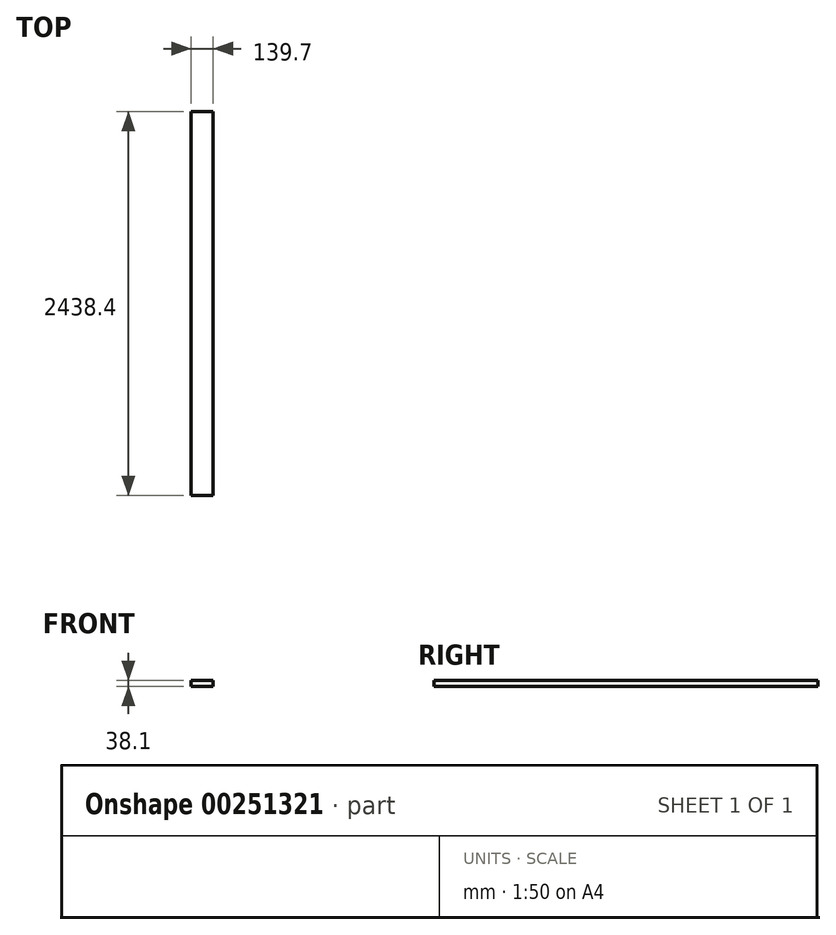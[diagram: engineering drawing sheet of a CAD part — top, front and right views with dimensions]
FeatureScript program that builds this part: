
annotation { "Feature Type Name" : "Feature", "Feature Type Description" : "" }
export const myFeature = defineFeature(function(context is Context, id is Id, definition is map)
    precondition{}
    {
        {
            var Q0;
            Q0=qCreatedBy(makeId("Top.planeOp"),FACE);
            var sketch = newSketch(context, id + "F0", { "sketchPlane" : qUnion([Q0])});
            skLineSegment(sketch, "E0.bottom", {"start": v(-75.42, 1896.16) * mm, "end": v(64.28, 1896.16) * mm});
            skLineSegment(sketch, "E0.top", {"start": v(-75.42, -542.24) * mm, "end": v(64.28, -542.24) * mm});
            skLineSegment(sketch, "E0.left", {"start": v(-75.42, 1896.16) * mm, "end": v(-75.42, -542.24) * mm});
            skLineSegment(sketch, "E0.right", {"start": v(64.28, 1896.16) * mm, "end": v(64.28, -542.24) * mm});
            skSolve(sketch);
        }
        {
            var Q0;
            Q0=makeQuery(id+"F0.imprint","IMPRINT",FACE,{"disambiguationData":[TD([[makeQuery(id+"F0.imprint","IMPRINT",EDGE,{"derivedFrom":sQuery(id+"F0.wireOp",EDGE,"E0.bottom")}),-1.0]])]});
            extrude(context, id + "F1", {"entities" : qUnion([Q0]), "depth" : 38.1 * mm});
        }
    });
